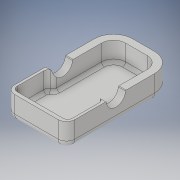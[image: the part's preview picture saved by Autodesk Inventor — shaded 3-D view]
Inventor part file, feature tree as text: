
AUTODESK INVENTOR PART (.ipt)
format: ipt  version: 2018 (Build 220112000, 112)  size: 232,448 bytes
history: native  units: mm
features: extrude x3, fillet x3, sketch x2, projected_geometry x1
ambient origin geometry x8: Origin, YZ Plane, XZ Plane, XY Plane, X Axis, Y Axis, Z Axis, Center Point
bodies: Solid1 (feature_tree)
feature tree (9):
  sketch  "Sketch1"  dims[d0=25.0mm d1=44.5mm]
  extrude  "Extrusion1"  Depth=25.0mm
  extrude  "Extrusion3"  Depth=0.25mm
  extrude  "Extrusion4"  Depth=0.25mm
  fillet  "Fillet1"  Radius=2.0mm
  fillet  "Fillet2"  Radius=3.0mm
  fillet  "Fillet3"  Radius=1.5mm
  sketch  "Sketch2"  dims[d2=8.0mm d3=3.5mm d4=5.0mm d5=2.0mm d6=3.0mm d7=1.5mm d8=1.0mm d9=1.0mm d10=3.0mm d11=3.0mm d12=4.0mm d13=4.0mm d14=11.0mm d15=10.0mm d16=0.0mm d19=8.0mm d20=0.0mm d21=8.0mm d22=24.0mm d23=10.0mm d24=78.5mm d25=0.0mm d26=1.25mm d27=3.0mm d28=0.25mm]
  projected_geometry  "Project Cut Edges1"
